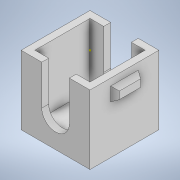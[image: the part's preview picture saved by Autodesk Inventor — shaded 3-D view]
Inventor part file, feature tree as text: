
AUTODESK INVENTOR PART (.ipt)
format: ipt  version: 2022 (Build 260153000, 153)  size: 138,240 bytes
history: native  units: in
note: dims shown in document units (in); Inventor stores cm internally (conversion verified against a paired STEP export)
features: sketch x9, extrude x4, shell x1
ambient origin geometry x8: Origin, YZ Plane, XZ Plane, XY Plane, X Axis, Y Axis, Z Axis, Center Point
bodies: Solid1 (feature_tree)
feature tree (14):
  extrude  "Extrusion1"  Depth=0.1969in
  shell  "Shell1"  Thickness=0.1969in
  extrude  "Extrusion3"  TaperAngle=0.0deg  [1 undecoded]
  sketch  "Sketch4"  dims[d10=0.0394in d11=0.0157in d12=-0.2061in]
  sketch  "Sketch5"  dims[d13=0.0394in d14=0.0787in]
  sketch  "Sketch6"  dims[d15=0.0394in]
  sketch  "Sketch7"  dims[d16=0.0787in]
  sketch  "Sketch8"  dims[d17=0.0394in]
  extrude  "Extrusion4"  Depth=0.0157in
  extrude  "Extrusion5"  Depth=0.0787in
  sketch  "Sketch1"  dims[d0=0.1969in d1=0.1969in d2=0.1969in d3=0.0in]
  sketch  "Sketch3"  dims[d4=0.0197in d8=0.0in d9=0.0in]
  sketch  "Sketch9"  dims[d18=0.0157in d19=-0.2061in]
  sketch  "Sketch10"
note: 1 required parameter value undecoded (feature->parameter linkage not recoverable at this tier; creation-order binding heuristic only, values carry confidence <= 0.55)
